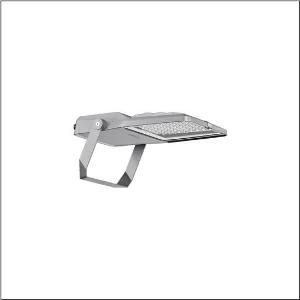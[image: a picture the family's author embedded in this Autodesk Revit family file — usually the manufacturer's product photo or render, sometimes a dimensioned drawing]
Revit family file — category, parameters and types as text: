
# Revit family: floodlight_fl_21_iq_mini___pl64_5xa7772d3e1a_da13
name_source: partatom
category: Lighting Fixtures
units: mm (PartAtom-declared; Revit-internal decimal feet)

## family parameters
Cut with Voids When Loaded = No
Host = Face
Light Source = No
Part Type = Normal
Room Calculation Point = No
Round Connector Dimension = Use Diameter
Shared = No

## types (1)
- --- (1 x LED, 14810 lm, 143 W, 3000K)
    Apparent Load = 143 VA
    CIE Flux Codes = 28 80 98 100 100
    Color Rendering = 80
    Color Temperature = 3000K
    Default Elevation = 1800 mm
    Description = Floodlight FL 21 iQ mini, floodlight, primary light control with lens, of PMMA, primary optical cover: protective disc, of toughened safety glass, transparent, light distribution: PL64, light emission: direct distribution, installation type: surface-mounted, LED, High Power LED, rated luminous flux: 14.810lm, luminous efficacy: 104lm/W, light colour: 830, colour temperature: 3000K, control: Street-Remote, Auto-Match, Temp-Guard, Night-Set, Smart-Wire, Desk-Remote (wireless, voltage-free reading and setting of iQ features in the workshop via application-optimized NFC function/RFID function), optimised constant luminous flux control (CLO 2.0), with terminal, 6-pole, mains connection: 220..240V, AC, 50/60Hz, start of lifetime: 143W, end of service life: 152W, reduction: 61W, luminaire housing, of diecast aluminium, powder-coated, Siteco® metallic grey (DB 702S), corrosivity category C5 mid according to DIN EN ISO 12944, sealing non-destructively replaceable, mounting bracket, of steel, galvanised, powder-coated, Siteco® metallic grey (DB 702S), protection rating (complete): IP66, insulation class (complete): insulation class II (safety insulation), certification: CE, ENEC, VDE, protection symbol: D, impact resistance: IK08, permissible operating ambient temperature: -40..+40°C, permissible operating ambient temperature for outdoor applications: -40..+50°C, standard: DIN EN 12944, LABS conformity tested according to VDMA 24364:2018-05, packaging unit: 1 piece

Light Distribution: PL64
    Height = 70 mm
    Lamp = 1 x LED
    Lamp Light Flux = 14810 lm
    Lamp Power = 143 W
    Lamp count = 1
    Length = 485 mm
    Luminous efficacy = 104 lm/W
    Manufacturer = Siteco
    ModVariant = No
    Model = 5XA7772D3E1A
    Number of Poles = 1
    OnlyDefault = Yes
    Power Factor = 1
    Product Name = Floodlight FL 21 iQ mini | PL64
    Product group = floodlight | pylon annexe
    ProductGroupID = 6200
    Protection Class = Protection class II
    Protection Degree = IP 66
    RLX_Detail_Level = 1
    RLX_Emergency_Light_Flux = 0 lm
    RLX_Emergency_Type = 0
    RLX_Emergency_Type_DB = No
    RlxData = <blob elided: 96401 chars, md5=10d68404>
    Socket = socket
    Standby Power = 0 W
    System Light Flux = 14810 lm
    System Power = 143 W
    Type Comments = factory setting: luminous flux: 100 % | dim-lin: 254 | 730 mA
    Type Image = l_1006845.jpg
    URL = http://relux.com
    VarID = @adj_098063
    Voltage = 0 V
    Weight = 0.00 kg
    Width = 337 mm

## geometry (parser evidence)
native form markers: Blend x4, Sweep x14
no freeform markers — native parametric forms only
